# Revit family: 304_0f38b157234b4585aaaac3afd88492
name_source: partatom
category: Pipe Accessories
units: mm (PartAtom-declared; Revit-internal decimal feet)

## family parameters
Always vertical = Yes
Cut with Voids When Loaded = No
Part Type = Valve - Breaks Into
Round Connector Dimension = Use Diameter
Shared = No
Work Plane-Based = No

## types (15) — shared parameters
CAT0 = Yes
Description = Automatic balancing valve
H1 = 118 mm  [stored 0.387139 ft]
H1__ve = -118 mm  [stored -0.387139 ft]
L = 170 mm  [stored 0.557743 ft]
L1 = 49 mm  [stored 0.160761 ft]
L2D = 170 mm  [stored 0.557743 ft]
L2D_Min = 3048 mm  [stored 10 ft]
LL = 85 mm  [stored 0.278871 ft]
Manufacturer = Frese A/S
QmdConnectorList = 301;D;302;D
URL = https://www.frese.eu
W2D = 100 mm  [stored 0.328084 ft]
magiPartTypeId = 304
magiProductFamilyId = 0f38b157234b4585aaaac3afd88492

## per-type parameters (varying)
| type | D | DC | DC2 | magiProductId |
| Frese ALPHA DN100 PN16 | 100 mm | 163 mm  [stored 0.534777 ft] | 82 mm | Frese ALPHA DN100 |
| Frese ALPHA DN125 PN16 | 125 mm | 193 mm  [stored 0.633202 ft] | 97 mm | Frese ALPHA DN125 |
| Frese ALPHA DN150 PN16 | 150 mm | 216 mm  [stored 0.708661 ft] | 108 mm  [stored 0.354331 ft] | Frese ALPHA DN150 |
| Frese ALPHA DN200 PN16 | 200 mm | 271 mm  [stored 0.889108 ft] | 136 mm | Frese ALPHA DN200 |
| Frese ALPHA DN250 PN16 | 200 mm | 271 mm  [stored 0.889108 ft] | 136 mm | Frese ALPHA DN250 |
| Frese ALPHA DN300 PN16 | 315 mm | 383 mm  [stored 1.25656 ft] | 192 mm | Frese ALPHA DN300 |
| Frese ALPHA DN350 PN16 | 355 mm | 443 mm  [stored 1.45341 ft] | 222 mm | Frese ALPHA DN350 |
| Frese ALPHA DN400 PN16 | 405 mm | 496 mm  [stored 1.6273 ft] | 248 mm  [stored 0.813648 ft] | Frese ALPHA DN400 |
| Frese ALPHA DN450 PN16 | 455 mm | 545 mm  [stored 1.78806 ft] | 273 mm | Frese ALPHA DN450 |
| Frese ALPHA DN50 PN16 | 80 mm | 100 mm  [stored 0.328084 ft] | 50 mm  [stored 0.164042 ft] | Frese ALPHA DN50 |
| Frese ALPHA DN500 PN16 | 508 mm | 601 mm  [stored 1.97178 ft] | 301 mm | Frese ALPHA DN500 |
| Frese ALPHA DN600 PN16 | 610 mm | 715 mm  [stored 2.3458 ft] | 358 mm | Frese ALPHA DN600 |
| Frese ALPHA DN65 PN16 | 80 mm | 119 mm  [stored 0.39042 ft] | 60 mm | Frese ALPHA DN65 |
| Frese ALPHA DN80 PN16 | 80 mm | 131 mm  [stored 0.42979 ft] | 66 mm  [stored 0.216535 ft] | Frese ALPHA DN80 |
| Frese ALPHA DN800 PN16 | 760 mm | 880 mm  [stored 2.88714 ft] | 440 mm  [stored 1.44357 ft] | Frese ALPHA DN800 |

note: column(s) folded — value = type name in every type: MC Product Code

note: [stored X ft] marks values corroborated as IEEE doubles in the binary element streams (Revit-internal decimal feet)

## geometry (parser evidence)
native form markers: Sweep x1
no freeform markers — native parametric forms only
